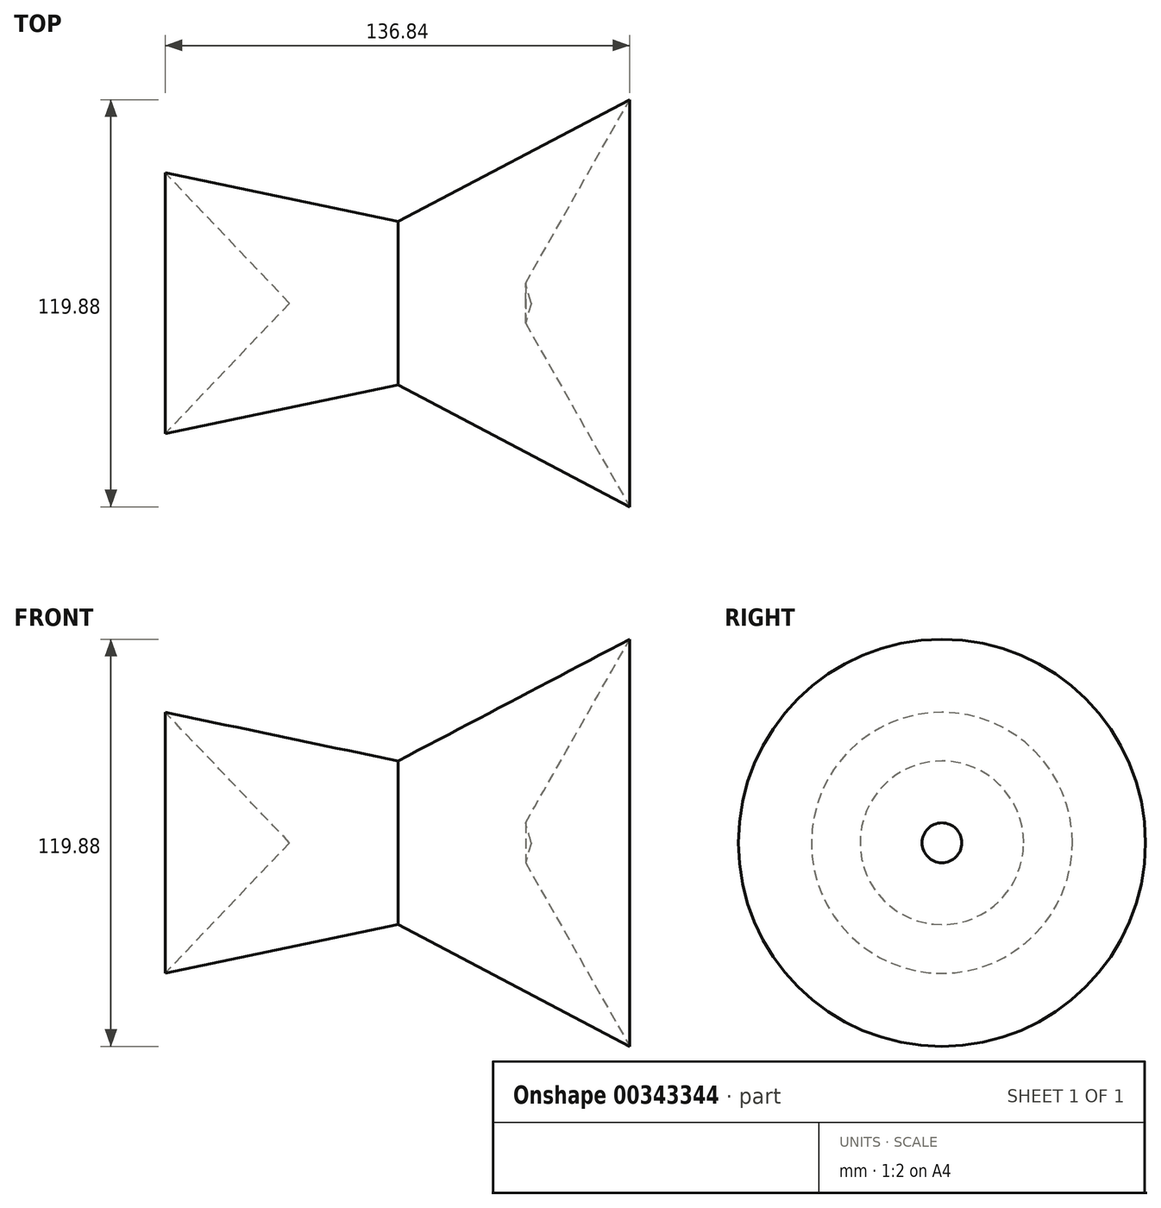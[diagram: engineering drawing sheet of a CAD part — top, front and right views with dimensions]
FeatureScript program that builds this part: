
annotation { "Feature Type Name" : "Feature", "Feature Type Description" : "" }
export const myFeature = defineFeature(function(context is Context, id is Id, definition is map)
    precondition{}
    {
        {
            var Q0;
            Q0=qCreatedBy(makeId("Top.planeOp"),FACE);
            var sketch = newSketch(context, id + "F0", { "sketchPlane" : qUnion([Q0])});
            skLineSegment(sketch, "E0", {"start": v(-68.31, 38.42) * mm, "end": v(-27.58, -4.32) * mm});
            skLineSegment(sketch, "E1", {"start": v(-27.58, -4.32) * mm, "end": v(-66.02, -46.2) * mm});
            skLineSegment(sketch, "E2", {"start": v(-66.02, -46.2) * mm, "end": v(0.25, -25.84) * mm});
            skLineSegment(sketch, "E3", {"start": v(0.25, -25.84) * mm, "end": v(55.05, -53.1) * mm});
            skLineSegment(sketch, "E4", {"start": v(55.05, -53.1) * mm, "end": v(37.83, 5.86) * mm});
            skLineSegment(sketch, "E5", {"start": v(37.83, 5.86) * mm, "end": v(68.53, 59.94) * mm});
            skLineSegment(sketch, "E6", {"start": v(68.53, 59.94) * mm, "end": v(0.25, 24.08) * mm});
            skLineSegment(sketch, "E7", {"start": v(0.25, 24.08) * mm, "end": v(-68.31, 38.42) * mm});
            skLineSegment(sketch, "E8", {"start": v(-50.5, 0) * mm, "end": v(45.9, 0) * mm});
            skSolve(sketch);
        }
        {
            var Q0;
            {var subQ0=sQuery(id+"F0.wireOp",EDGE,"E5");Q0=makeQuery(id+"F0.imprint","IMPRINT",FACE,{"disambiguationData":[TD([[makeQuery(id+"F0.imprint","IMPRINT",EDGE,{"derivedFrom":subQ0}),1.0]])]});}
            var Q1;
            Q1=sQuery(id+"F0.wireOp",EDGE,"E8");
            revolve(context, id + "F1", {"entities" : qUnion([Q0]), "axis" : qUnion([Q1]), "revolveType" : RevolveType.FULL});
        }
    });
